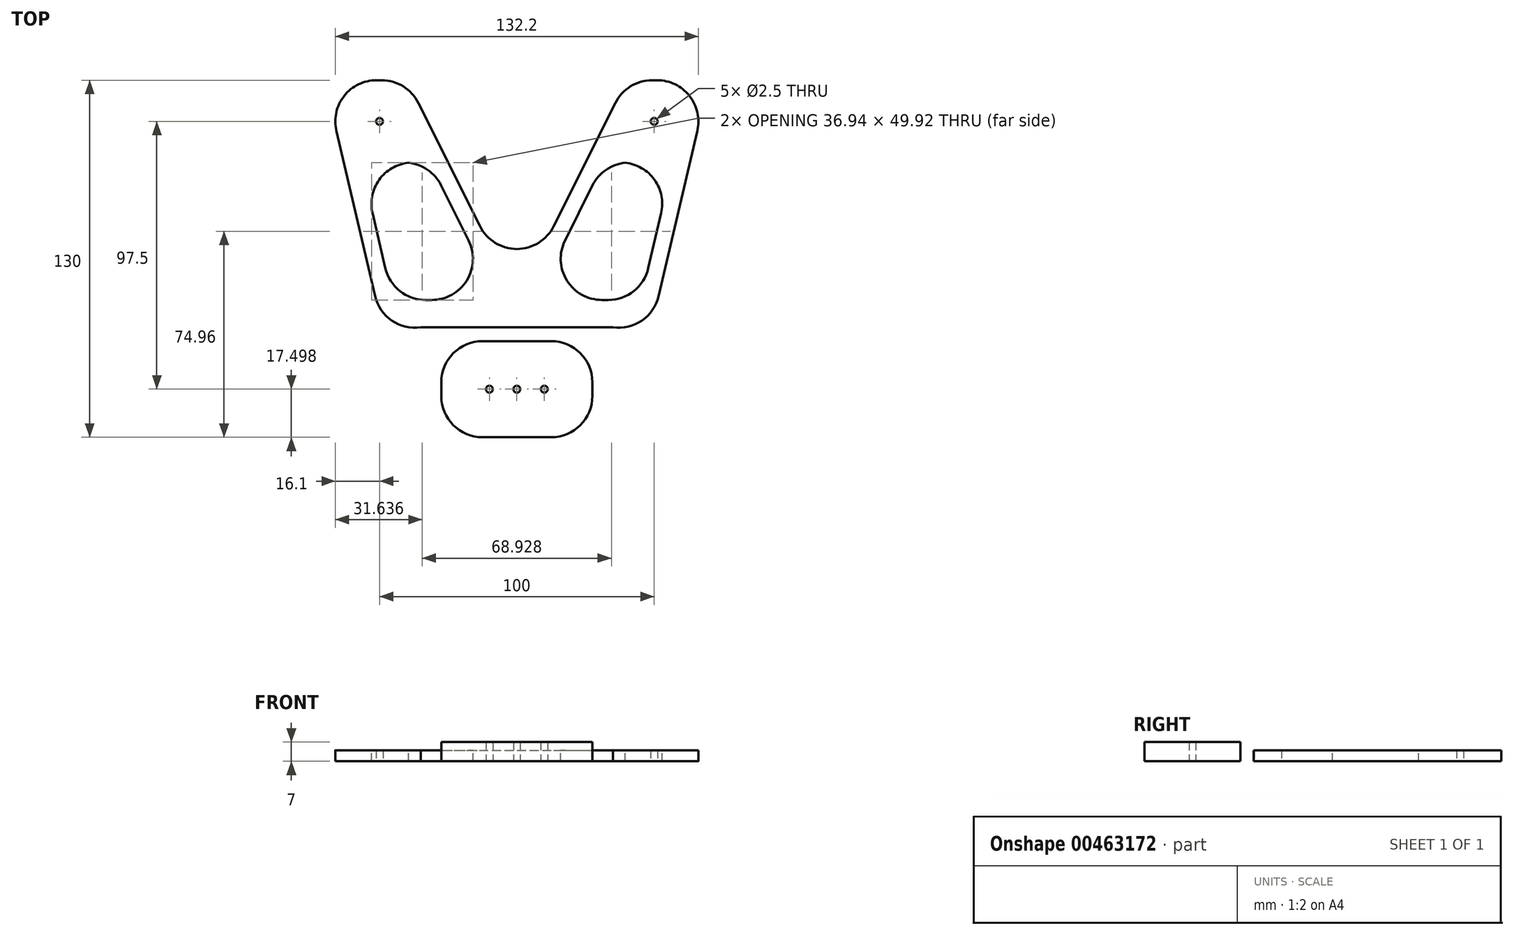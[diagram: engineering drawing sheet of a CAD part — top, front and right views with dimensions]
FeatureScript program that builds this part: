
annotation { "Feature Type Name" : "Feature", "Feature Type Description" : "" }
export const myFeature = defineFeature(function(context is Context, id is Id, definition is map)
    precondition{}
    {
        {
            var Q0;
            Q0=qCreatedBy(makeId("Top.planeOp"),FACE);
            var sketch = newSketch(context, id + "F0", { "sketchPlane" : qUnion([Q0])});
            skLineSegment(sketch, "E0.bottom", {"start": v(-70, 93.34) * mm, "end": v(70, 93.34) * mm});
            skLineSegment(sketch, "E0.top", {"start": v(-70, -56.66) * mm, "end": v(70, -56.66) * mm});
            skLineSegment(sketch, "E0.left", {"start": v(-70, 93.34) * mm, "end": v(-70, -56.66) * mm});
            skLineSegment(sketch, "E0.right", {"start": v(70, 93.34) * mm, "end": v(70, -56.66) * mm});
            skLineSegment(sketch, "E1.bottom", {"start": v(-35, -56.66) * mm, "end": v(35, -56.66) * mm});
            skLineSegment(sketch, "E1.top", {"start": v(-35, 3.34) * mm, "end": v(35, 3.34) * mm});
            skLineSegment(sketch, "E1.left", {"start": v(-35, -56.66) * mm, "end": v(-35, 3.34) * mm});
            skLineSegment(sketch, "E1.right", {"start": v(35, -56.66) * mm, "end": v(35, 3.34) * mm});
            skLineSegment(sketch, "E2", {"start": v(-70, 93.34) * mm, "end": v(-35, -56.66) * mm});
            skLineSegment(sketch, "E3", {"start": v(70, 93.34) * mm, "end": v(35, -56.66) * mm});
            skLineSegment(sketch, "E4.bottom", {"start": v(-27.5, -1.66) * mm, "end": v(27.5, -1.66) * mm});
            skLineSegment(sketch, "E4.top", {"start": v(-27.5, -36.66) * mm, "end": v(27.5, -36.66) * mm});
            skLineSegment(sketch, "E4.left", {"start": v(-27.5, -1.66) * mm, "end": v(-27.5, -36.66) * mm});
            skLineSegment(sketch, "E4.right", {"start": v(27.5, -1.66) * mm, "end": v(27.5, -36.66) * mm});
            skLineSegment(sketch, "E5", {"start": v(-40, 93.34) * mm, "end": v(0, 13.34) * mm});
            skLineSegment(sketch, "E6", {"start": v(0, 13.34) * mm, "end": v(40, 93.34) * mm});
            skLineSegment(sketch, "E7", {"start": v(40, 93.34) * mm, "end": v(-40, 93.34) * mm});
            skCircle(sketch, "E8", {"center": v(-10, -19.16) * mm, "radius": 1.25 * mm});
            skCircle(sketch, "E9", {"center": v(0, -19.16) * mm, "radius": 1.25 * mm});
            skCircle(sketch, "E10", {"center": v(10, -19.16) * mm, "radius": 1.25 * mm});
            skCircle(sketch, "E11", {"center": v(50, 78.34) * mm, "radius": 1.25 * mm});
            skCircle(sketch, "E12", {"center": v(-50, 78.34) * mm, "radius": 1.25 * mm});
            skLineSegment(sketch, "E13", {"start": v(31.7, 63.34) * mm, "end": v(56.84, 63.34) * mm});
            skLineSegment(sketch, "E14", {"start": v(56.84, 63.34) * mm, "end": v(45.17, 13.34) * mm});
            skLineSegment(sketch, "E15", {"start": v(45.17, 13.34) * mm, "end": v(6.7, 13.34) * mm});
            skLineSegment(sketch, "E16", {"start": v(6.7, 13.34) * mm, "end": v(31.7, 63.34) * mm});
            skLineSegment(sketch, "E17", {"start": v(-56.84, 63.34) * mm, "end": v(-31.7, 63.34) * mm});
            skLineSegment(sketch, "E18", {"start": v(-31.7, 63.34) * mm, "end": v(-6.7, 13.34) * mm});
            skLineSegment(sketch, "E19", {"start": v(-6.7, 13.34) * mm, "end": v(-45.17, 13.34) * mm});
            skLineSegment(sketch, "E20", {"start": v(-45.17, 13.34) * mm, "end": v(-56.84, 63.34) * mm});
            skSolve(sketch);
        }
        {
            var Q0;
            Q0=makeQuery(id+"F0.imprint","IMPRINT",FACE,{"disambiguationData":[TD([[makeQuery(id+"F0.imprint","IMPRINT",EDGE,{"derivedFrom":sQuery(id+"F0.wireOp",EDGE,"E0.bottom")}),-1.0]])]});
            var Q1;
            Q1=makeQuery(id+"F0.imprint","IMPRINT",FACE,{"disambiguationData":[TD([[makeQuery(id+"F0.imprint","IMPRINT",EDGE,{"derivedFrom":sQuery(id+"F0.wireOp",EDGE,"E1.bottom")}),1.0]])]});
            var Q2;
            Q2=makeQuery(id+"F0.imprint","IMPRINT",FACE,{"disambiguationData":[TD([[makeQuery(id+"F0.imprint","IMPRINT",EDGE,{"derivedFrom":sQuery(id+"F0.wireOp",EDGE,"E4.bottom")}),-1.0]])]});
            extrude(context, id + "F1", {"entities" : qUnion([Q0, Q1, Q2]), "depth" : 4 * mm});
        }
        {
            var Q0;
            Q0=makeQuery(id+"F0.imprint","IMPRINT",FACE,{"disambiguationData":[TD([[makeQuery(id+"F0.imprint","IMPRINT",EDGE,{"derivedFrom":sQuery(id+"F0.wireOp",EDGE,"E4.bottom")}),-1.0]])]});
            extrude(context, id + "F2", {"entities" : qUnion([Q0]), "operationType" : NewBodyOperationType.ADD, "depth" : 7 * mm});
        }
        {
            var Q0;
            Q0=makeQuery(id+"F1.opExtrude","SWEPT_EDGE",EDGE,{"disambiguationData":[OSD([sQuery(id+"F0.wireOp",EDGE,"E5"),sQuery(id+"F0.wireOp",EDGE,"E6")])]});
            var Q1;
            Q1=makeQuery(id+"F1.opExtrude","SWEPT_EDGE",EDGE,{"disambiguationData":[OSD([sQuery(id+"F0.wireOp",EDGE,"E0.bottom"),sQuery(id+"F0.wireOp",EDGE,"E6"),sQuery(id+"F0.wireOp",EDGE,"E7")])]});
            var Q2;
            Q2=makeQuery(id+"F1.opExtrude","SWEPT_EDGE",EDGE,{"disambiguationData":[OSD([sQuery(id+"F0.wireOp",EDGE,"E0.bottom"),sQuery(id+"F0.wireOp",EDGE,"E0.right"),sQuery(id+"F0.wireOp",EDGE,"E3")])]});
            var Q3;
            Q3=makeQuery(id+"F1.opExtrude","SWEPT_EDGE",EDGE,{"disambiguationData":[OSD([sQuery(id+"F0.wireOp",EDGE,"E0.bottom"),sQuery(id+"F0.wireOp",EDGE,"E0.left"),sQuery(id+"F0.wireOp",EDGE,"E2")])]});
            var Q4;
            Q4=makeQuery(id+"F1.opExtrude","SWEPT_EDGE",EDGE,{"disambiguationData":[OSD([sQuery(id+"F0.wireOp",EDGE,"E0.bottom"),sQuery(id+"F0.wireOp",EDGE,"E5"),sQuery(id+"F0.wireOp",EDGE,"E7")])]});
            var Q5;
            Q5=makeQuery(id+"F2.opExtrude","SWEPT_EDGE",EDGE,{"disambiguationData":[OSD([sQuery(id+"F0.wireOp",EDGE,"E4.bottom"),sQuery(id+"F0.wireOp",EDGE,"E4.right")])]});
            var Q6;
            Q6=makeQuery(id+"F2.opExtrude","SWEPT_EDGE",EDGE,{"disambiguationData":[OSD([sQuery(id+"F0.wireOp",EDGE,"E4.bottom"),sQuery(id+"F0.wireOp",EDGE,"E4.left")])]});
            var Q7;
            Q7=makeQuery(id+"F2.opExtrude","SWEPT_EDGE",EDGE,{"disambiguationData":[OSD([sQuery(id+"F0.wireOp",EDGE,"E4.top"),sQuery(id+"F0.wireOp",EDGE,"E4.right")])]});
            var Q8;
            Q8=makeQuery(id+"F2.opExtrude","SWEPT_EDGE",EDGE,{"disambiguationData":[OSD([sQuery(id+"F0.wireOp",EDGE,"E4.top"),sQuery(id+"F0.wireOp",EDGE,"E4.left")])]});
            var Q9;
            Q9=makeQuery(id+"F1.opExtrude","SWEPT_EDGE",EDGE,{"disambiguationData":[OSD([sQuery(id+"F0.wireOp",EDGE,"E0.top"),sQuery(id+"F0.wireOp",EDGE,"E1.bottom"),sQuery(id+"F0.wireOp",EDGE,"E1.left"),sQuery(id+"F0.wireOp",EDGE,"E2")])]});
            var Q10;
            Q10=makeQuery(id+"F1.opExtrude","SWEPT_EDGE",EDGE,{"disambiguationData":[OSD([sQuery(id+"F0.wireOp",EDGE,"E0.top"),sQuery(id+"F0.wireOp",EDGE,"E1.bottom"),sQuery(id+"F0.wireOp",EDGE,"E1.right"),sQuery(id+"F0.wireOp",EDGE,"E3")])]});
            var Q11;
            Q11=makeQuery(id+"F1.opExtrude","SWEPT_EDGE",EDGE,{"disambiguationData":[OSD([sQuery(id+"F0.wireOp",EDGE,"E15"),sQuery(id+"F0.wireOp",EDGE,"E16")])]});
            var Q12;
            Q12=makeQuery(id+"F1.opExtrude","SWEPT_EDGE",EDGE,{"disambiguationData":[OSD([sQuery(id+"F0.wireOp",EDGE,"E14"),sQuery(id+"F0.wireOp",EDGE,"E15")])]});
            var Q13;
            Q13=makeQuery(id+"F1.opExtrude","SWEPT_EDGE",EDGE,{"disambiguationData":[OSD([sQuery(id+"F0.wireOp",EDGE,"E18"),sQuery(id+"F0.wireOp",EDGE,"E19")])]});
            var Q14;
            Q14=makeQuery(id+"F1.opExtrude","SWEPT_EDGE",EDGE,{"disambiguationData":[OSD([sQuery(id+"F0.wireOp",EDGE,"E19"),sQuery(id+"F0.wireOp",EDGE,"E20")])]});
            var Q15;
            Q15=makeQuery(id+"F1.opExtrude","SWEPT_EDGE",EDGE,{"disambiguationData":[OSD([sQuery(id+"F0.wireOp",EDGE,"E17"),sQuery(id+"F0.wireOp",EDGE,"E20")])]});
            var Q16;
            Q16=makeQuery(id+"F1.opExtrude","SWEPT_EDGE",EDGE,{"disambiguationData":[OSD([sQuery(id+"F0.wireOp",EDGE,"E17"),sQuery(id+"F0.wireOp",EDGE,"E18")])]});
            var Q17;
            Q17=makeQuery(id+"F1.opExtrude","SWEPT_EDGE",EDGE,{"disambiguationData":[OSD([sQuery(id+"F0.wireOp",EDGE,"E13"),sQuery(id+"F0.wireOp",EDGE,"E16")])]});
            var Q18;
            Q18=makeQuery(id+"F1.opExtrude","SWEPT_EDGE",EDGE,{"disambiguationData":[OSD([sQuery(id+"F0.wireOp",EDGE,"E13"),sQuery(id+"F0.wireOp",EDGE,"E14")])]});
            fillet(context, id + "F3", {"entities" : qUnion([Q0, Q1, Q2, Q3, Q4, Q5, Q6, Q7, Q8, Q9, Q10, Q11, Q12, Q13, Q14, Q15, Q16, Q17, Q18]), "radius" : 15 * mm, "tangentPropagation" : true, "allowEdgeOverflow" : false});
        }
    });
